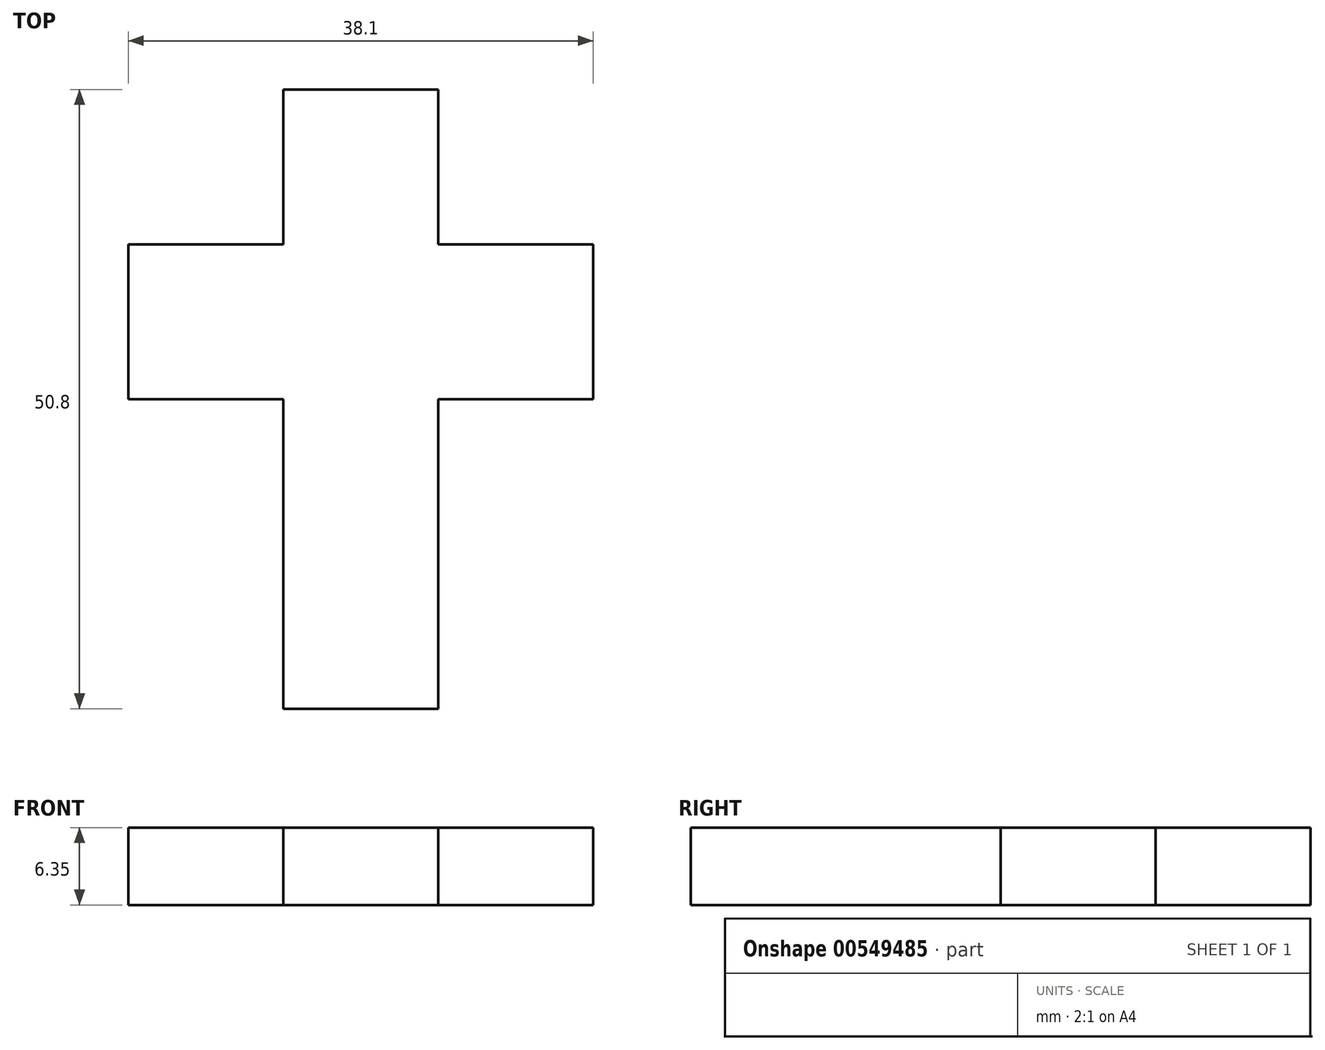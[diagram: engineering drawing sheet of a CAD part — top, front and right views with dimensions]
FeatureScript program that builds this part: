
annotation { "Feature Type Name" : "Feature", "Feature Type Description" : "" }
export const myFeature = defineFeature(function(context is Context, id is Id, definition is map)
    precondition{}
    {
        {
            var Q0;
            Q0=qCreatedBy(makeId("Top.planeOp"),FACE);
            var sketch = newSketch(context, id + "F0", { "sketchPlane" : qUnion([Q0])});
            skLineSegment(sketch, "E0.bottom", {"start": v(0, 0) * mm, "end": v(12.7, 0) * mm});
            skLineSegment(sketch, "E0.top", {"start": v(0, 50.8) * mm, "end": v(12.7, 50.8) * mm});
            skLineSegment(sketch, "E0.left", {"start": v(0, 0) * mm, "end": v(0, 50.8) * mm});
            skLineSegment(sketch, "E0.right", {"start": v(12.7, 0) * mm, "end": v(12.7, 50.8) * mm});
            skLineSegment(sketch, "E1.bottom", {"start": v(-12.7, 38.1) * mm, "end": v(25.4, 38.1) * mm});
            skLineSegment(sketch, "E1.top", {"start": v(-12.7, 25.4) * mm, "end": v(25.4, 25.4) * mm});
            skLineSegment(sketch, "E1.left", {"start": v(-12.7, 38.1) * mm, "end": v(-12.7, 25.4) * mm});
            skLineSegment(sketch, "E1.right", {"start": v(25.4, 38.1) * mm, "end": v(25.4, 25.4) * mm});
            skSolve(sketch);
        }
        {
            var Q0;
            Q0 = qSketchRegion(id + "F0", true);
            extrude(context, id + "F1", {"entities" : qUnion([Q0]), "depth" : 6.35 * mm, "offsetDistance" : 25.4 * mm});
        }
    });
